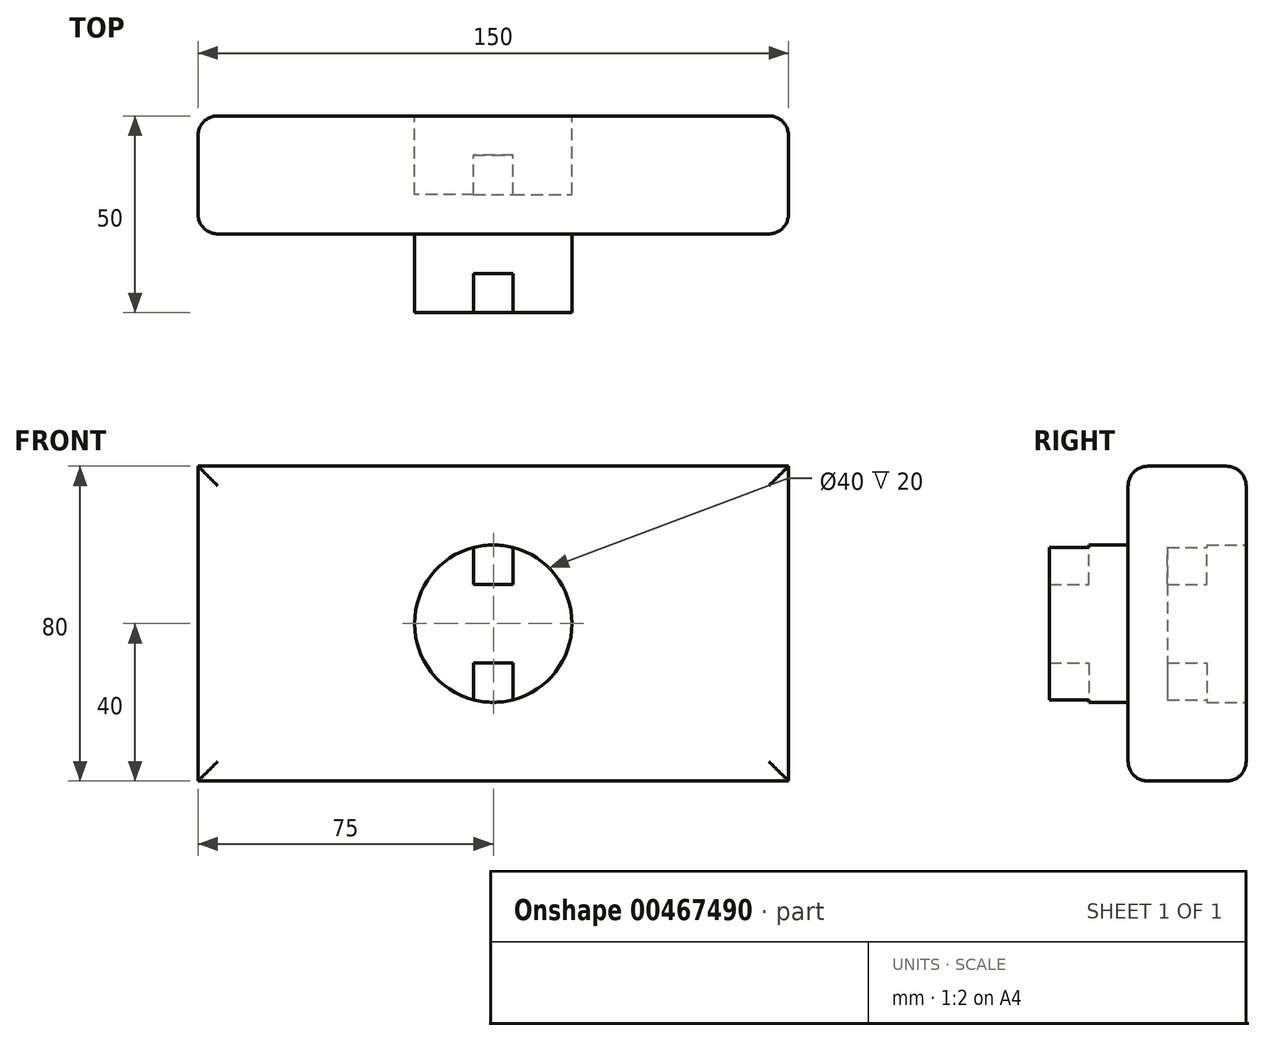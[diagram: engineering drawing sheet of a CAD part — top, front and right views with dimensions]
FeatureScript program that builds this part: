
annotation { "Feature Type Name" : "Feature", "Feature Type Description" : "" }
export const myFeature = defineFeature(function(context is Context, id is Id, definition is map)
    precondition{}
    {
        {
            var Q0;
            Q0=qCreatedBy(makeId("Top.planeOp"),FACE);
            var sketch = newSketch(context, id + "F0", { "sketchPlane" : qUnion([Q0])});
            skLineSegment(sketch, "E0.bottom", {"start": v(75, -15) * mm, "end": v(-75, -15) * mm});
            skLineSegment(sketch, "E0.top", {"start": v(75, 15) * mm, "end": v(-75, 15) * mm});
            skLineSegment(sketch, "E0.left", {"start": v(75, -15) * mm, "end": v(75, 15) * mm});
            skLineSegment(sketch, "E0.right", {"start": v(-75, -15) * mm, "end": v(-75, 15) * mm});
            skPoint(sketch, "E0.middle", {"position": v(0, 0) * mm});
            skSolve(sketch);
        }
        {
            var Q0;
            Q0=makeQuery(id+"F0.imprint","IMPRINT",FACE,{"disambiguationData":[TD([[makeQuery(id+"F0.imprint","IMPRINT",EDGE,{"derivedFrom":sQuery(id+"F0.wireOp",EDGE,"E0.bottom")}),-1.0]])]});
            extrude(context, id + "F1", {"entities" : qUnion([Q0]), "depth" : 80 * mm});
        }
        {
            var Q0;
            Q0=makeQuery(id+"F1.opExtrude","SWEPT_FACE",FACE,{"disambiguationData":[OSD([sQuery(id+"F0.wireOp",EDGE,"E0.bottom")])]});
            var sketch = newSketch(context, id + "F2", { "sketchPlane" : qUnion([Q0])});
            skCircle(sketch, "E1", {"center": v(0, 40) * mm, "radius": 20 * mm});
            skPoint(sketch, "E1.centerSnap0", {"position": v(75, 40) * mm});
            skPoint(sketch, "E1.centerSnap1", {"position": v(0, 80) * mm});
            skLineSegment(sketch, "E2", {"start": v(0, 60) * mm, "end": v(0, 50) * mm});
            skLineSegment(sketch, "E3", {"start": v(0, 50) * mm, "end": v(5, 50) * mm});
            skLineSegment(sketch, "E4", {"start": v(5, 50) * mm, "end": v(5, 59.36) * mm});
            skLineSegment(sketch, "E5", {"start": v(0, 50) * mm, "end": v(-5, 50) * mm});
            skLineSegment(sketch, "E6", {"start": v(-5, 50) * mm, "end": v(-5, 59.36) * mm});
            skLineSegment(sketch, "E7", {"start": v(0, 20) * mm, "end": v(0, 30) * mm});
            skLineSegment(sketch, "E8", {"start": v(0, 30) * mm, "end": v(5, 30) * mm});
            skLineSegment(sketch, "E9", {"start": v(5, 30) * mm, "end": v(5, 20.64) * mm});
            skLineSegment(sketch, "E10", {"start": v(0, 30) * mm, "end": v(-5, 30) * mm});
            skLineSegment(sketch, "E11", {"start": v(-5, 30) * mm, "end": v(-5, 20.64) * mm});
            skSolve(sketch);
        }
        {
            var Q0;
            Q0=makeQuery(id+"F2.imprint","IMPRINT",FACE,{"disambiguationData":[TD([[makeQuery(id+"F2.imprint","IMPRINT",EDGE,{"derivedFrom":sQuery(id+"F2.wireOp",EDGE,"E3")}),-1.0]])]});
            extrude(context, id + "F3", {"entities" : qUnion([Q0]), "operationType" : NewBodyOperationType.ADD, "depth" : 20 * mm});
        }
        {
            var Q0;
            {var subQ0=sQuery(id+"F2.wireOp",EDGE,"E2");Q0=makeQuery(id+"F2.imprint","IMPRINT",FACE,{"disambiguationData":[TD([[makeQuery(id+"F2.imprint","IMPRINT",EDGE,{"derivedFrom":subQ0}),1.0]])]});}
            var Q1;
            {var subQ0=sQuery(id+"F2.wireOp",EDGE,"E2");Q1=makeQuery(id+"F2.imprint","IMPRINT",FACE,{"disambiguationData":[TD([[makeQuery(id+"F2.imprint","IMPRINT",EDGE,{"derivedFrom":subQ0}),-1.0]])]});}
            var Q2;
            {var subQ0=sQuery(id+"F2.wireOp",EDGE,"E7");Q2=makeQuery(id+"F2.imprint","IMPRINT",FACE,{"disambiguationData":[TD([[makeQuery(id+"F2.imprint","IMPRINT",EDGE,{"derivedFrom":subQ0}),-1.0]])]});}
            var Q3;
            {var subQ0=sQuery(id+"F2.wireOp",EDGE,"E7");Q3=makeQuery(id+"F2.imprint","IMPRINT",FACE,{"disambiguationData":[TD([[makeQuery(id+"F2.imprint","IMPRINT",EDGE,{"derivedFrom":subQ0}),1.0]])]});}
            extrude(context, id + "F4", {"entities" : qUnion([Q0, Q1, Q2, Q3]), "operationType" : NewBodyOperationType.ADD, "depth" : 10 * mm});
        }
        {
            var Q0;
            Q0=makeQuery(id+"F1.opExtrude","CAP_EDGE",EDGE,{"disambiguationData":[OSD([sQuery(id+"F0.wireOp",EDGE,"E0.bottom")])],"isStart":false});
            var Q1;
            Q1=makeQuery(id+"F1.opExtrude","CAP_EDGE",EDGE,{"disambiguationData":[OSD([sQuery(id+"F0.wireOp",EDGE,"E0.top")])],"isStart":false});
            var Q2;
            Q2=makeQuery(id+"F1.opExtrude","CAP_EDGE",EDGE,{"disambiguationData":[OSD([sQuery(id+"F0.wireOp",EDGE,"E0.bottom")])],"isStart":true});
            var Q3;
            Q3=makeQuery(id+"F1.opExtrude","CAP_EDGE",EDGE,{"disambiguationData":[OSD([sQuery(id+"F0.wireOp",EDGE,"E0.top")])],"isStart":true});
            var Q4;
            Q4=makeQuery(id+"F1.opExtrude","SWEPT_EDGE",EDGE,{"disambiguationData":[OSD([sQuery(id+"F0.wireOp",EDGE,"E0.bottom"),sQuery(id+"F0.wireOp",EDGE,"E0.left")])]});
            var Q5;
            Q5=makeQuery(id+"F1.opExtrude","SWEPT_EDGE",EDGE,{"disambiguationData":[OSD([sQuery(id+"F0.wireOp",EDGE,"E0.top"),sQuery(id+"F0.wireOp",EDGE,"E0.left")])]});
            var Q6;
            Q6=makeQuery(id+"F1.opExtrude","SWEPT_EDGE",EDGE,{"disambiguationData":[OSD([sQuery(id+"F0.wireOp",EDGE,"E0.bottom"),sQuery(id+"F0.wireOp",EDGE,"E0.right")])]});
            var Q7;
            Q7=makeQuery(id+"F1.opExtrude","SWEPT_EDGE",EDGE,{"disambiguationData":[OSD([sQuery(id+"F0.wireOp",EDGE,"E0.top"),sQuery(id+"F0.wireOp",EDGE,"E0.right")])]});
            fillet(context, id + "F5", {"entities" : qUnion([Q0, Q1, Q2, Q3, Q4, Q5, Q6, Q7]), "radius" : 5 * mm, "tangentPropagation" : true, "allowEdgeOverflow" : false});
        }
        {
            var Q0;
            Q0=makeQuery(id+"F1.opExtrude","SWEPT_FACE",FACE,{"disambiguationData":[OSD([sQuery(id+"F0.wireOp",EDGE,"E0.top")])]});
            var sketch = newSketch(context, id + "F6", { "sketchPlane" : qUnion([Q0])});
            skCircle(sketch, "E12", {"center": v(0, 40) * mm, "radius": 20 * mm});
            skPoint(sketch, "E12.centerSnap0", {"position": v(70, 40) * mm});
            skLineSegment(sketch, "E13", {"start": v(0, 60) * mm, "end": v(0, 50) * mm});
            skLineSegment(sketch, "E14", {"start": v(0, 50) * mm, "end": v(5, 50) * mm});
            skLineSegment(sketch, "E15", {"start": v(5, 50) * mm, "end": v(5, 59.36) * mm});
            skLineSegment(sketch, "E16", {"start": v(0, 50) * mm, "end": v(-5, 50) * mm});
            skLineSegment(sketch, "E17", {"start": v(-5, 50) * mm, "end": v(-5, 59.36) * mm});
            skLineSegment(sketch, "E18", {"start": v(0, 20) * mm, "end": v(0, 30) * mm});
            skLineSegment(sketch, "E19", {"start": v(0, 30) * mm, "end": v(5, 30) * mm});
            skLineSegment(sketch, "E20", {"start": v(5, 30) * mm, "end": v(5, 20.64) * mm});
            skLineSegment(sketch, "E21", {"start": v(0, 30) * mm, "end": v(-5, 30) * mm});
            skLineSegment(sketch, "E22", {"start": v(-5, 30) * mm, "end": v(-5, 20.64) * mm});
            skArc(sketch, "E23", {"start": v(-5, 20.64) * mm, "mid": v(0, 20) * mm, "end": v(5, 20.64) * mm});
            skArc(sketch, "E24", {"start": v(5, 59.36) * mm, "mid": v(0, 60) * mm, "end": v(-5, 59.36) * mm});
            skSolve(sketch);
        }
        {
            var Q0;
            Q0=makeQuery(id+"F6.imprint","IMPRINT",FACE,{"disambiguationData":[TD([[makeQuery(id+"F6.imprint","IMPRINT",EDGE,{"derivedFrom":sQuery(id+"F6.wireOp",EDGE,"E14")}),-1.0]])]});
            extrude(context, id + "F7", {"entities" : qUnion([Q0]), "operationType" : NewBodyOperationType.REMOVE, "oppositeDirection" : true, "depth" : 20 * mm});
        }
        {
            var Q0;
            {var subQ0=sQuery(id+"F6.wireOp",EDGE,"E13");Q0=makeQuery(id+"F6.imprint","IMPRINT",FACE,{"disambiguationData":[TD([[makeQuery(id+"F6.imprint","IMPRINT",EDGE,{"derivedFrom":subQ0}),1.0]])]});}
            var Q1;
            {var subQ0=sQuery(id+"F6.wireOp",EDGE,"E13");Q1=makeQuery(id+"F6.imprint","IMPRINT",FACE,{"disambiguationData":[TD([[makeQuery(id+"F6.imprint","IMPRINT",EDGE,{"derivedFrom":subQ0}),-1.0]])]});}
            var Q2;
            {var subQ0=sQuery(id+"F6.wireOp",EDGE,"E18");Q2=makeQuery(id+"F6.imprint","IMPRINT",FACE,{"disambiguationData":[TD([[makeQuery(id+"F6.imprint","IMPRINT",EDGE,{"derivedFrom":subQ0}),-1.0]])]});}
            var Q3;
            {var subQ0=sQuery(id+"F6.wireOp",EDGE,"E18");Q3=makeQuery(id+"F6.imprint","IMPRINT",FACE,{"disambiguationData":[TD([[makeQuery(id+"F6.imprint","IMPRINT",EDGE,{"derivedFrom":subQ0}),1.0]])]});}
            extrude(context, id + "F8", {"entities" : qUnion([Q0, Q1, Q2, Q3]), "operationType" : NewBodyOperationType.REMOVE, "oppositeDirection" : true, "depth" : 10 * mm});
        }
    });
